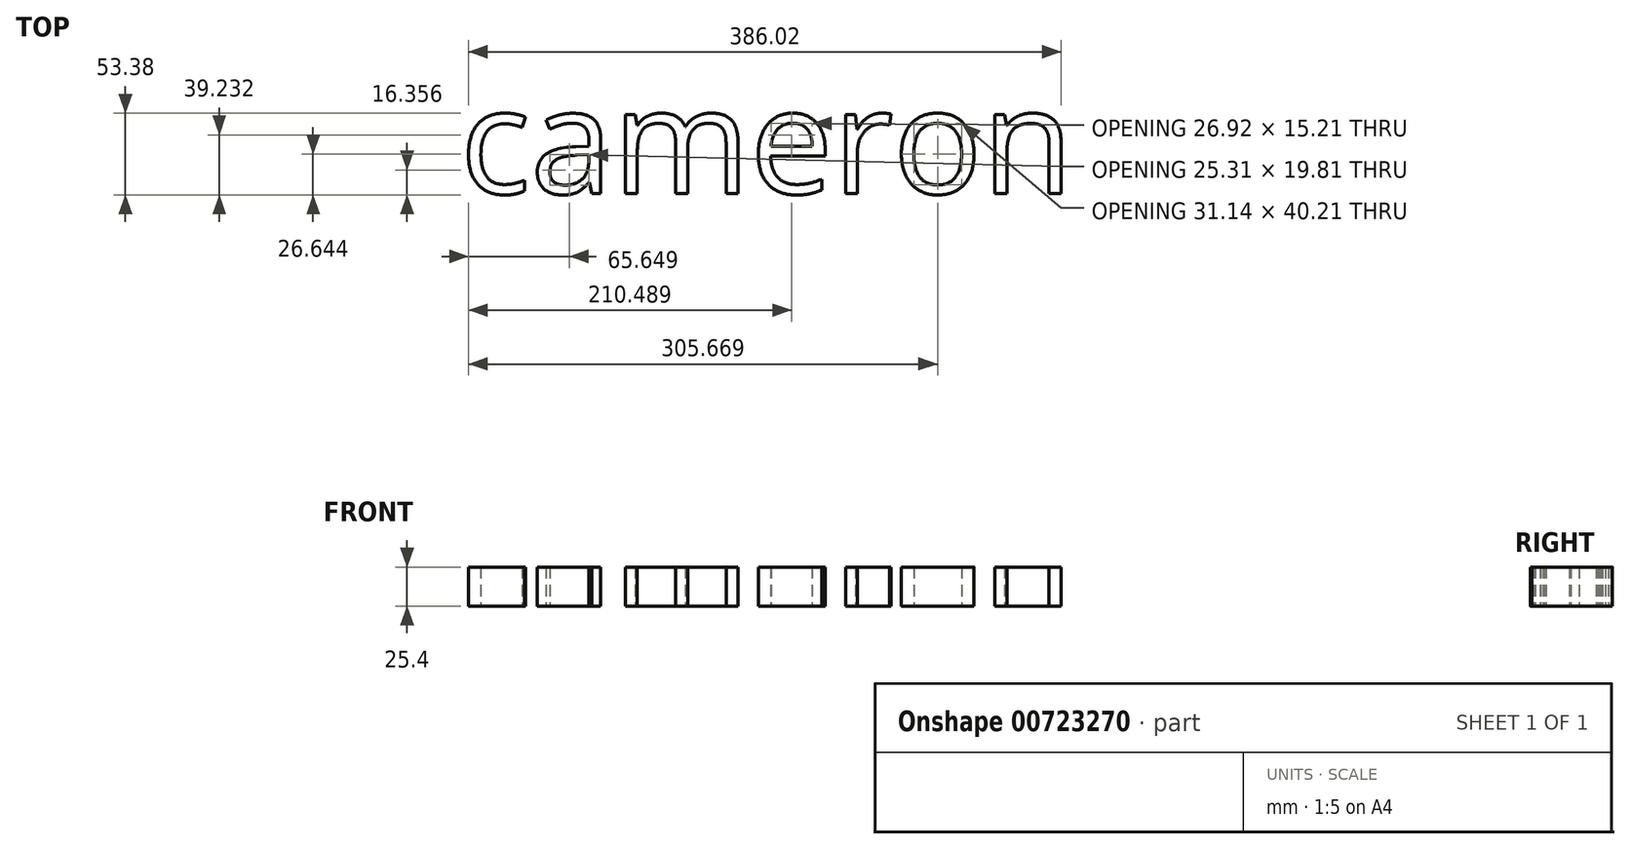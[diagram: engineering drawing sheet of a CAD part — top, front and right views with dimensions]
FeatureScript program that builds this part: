
annotation { "Feature Type Name" : "Feature", "Feature Type Description" : "" }
export const myFeature = defineFeature(function(context is Context, id is Id, definition is map)
    precondition{}
    {
        {
            var Q0;
            Q0=qCreatedBy(makeId("Top.planeOp"),FACE);
            var sketch = newSketch(context, id + "F0", { "sketchPlane" : qUnion([Q0])});
            skText(sketch, "E0", { "text": "cameron", "fontName": "OpenSans-Regular.ttf"});
            const initialGuessF0  = {"E0": [-0.21577, -0.04767, 1, 0, 0.06926]};
            skSetInitialGuess(sketch, initialGuessF0);
            skSolve(sketch);
        }
        {
            var Q0;
            Q0 = qSketchRegion(id + "F0", true);
            extrude(context, id + "F1", {"entities" : qUnion([Q0]), "depth" : 25.4 * mm, "offsetDistance" : 25.4 * mm});
        }
    });
